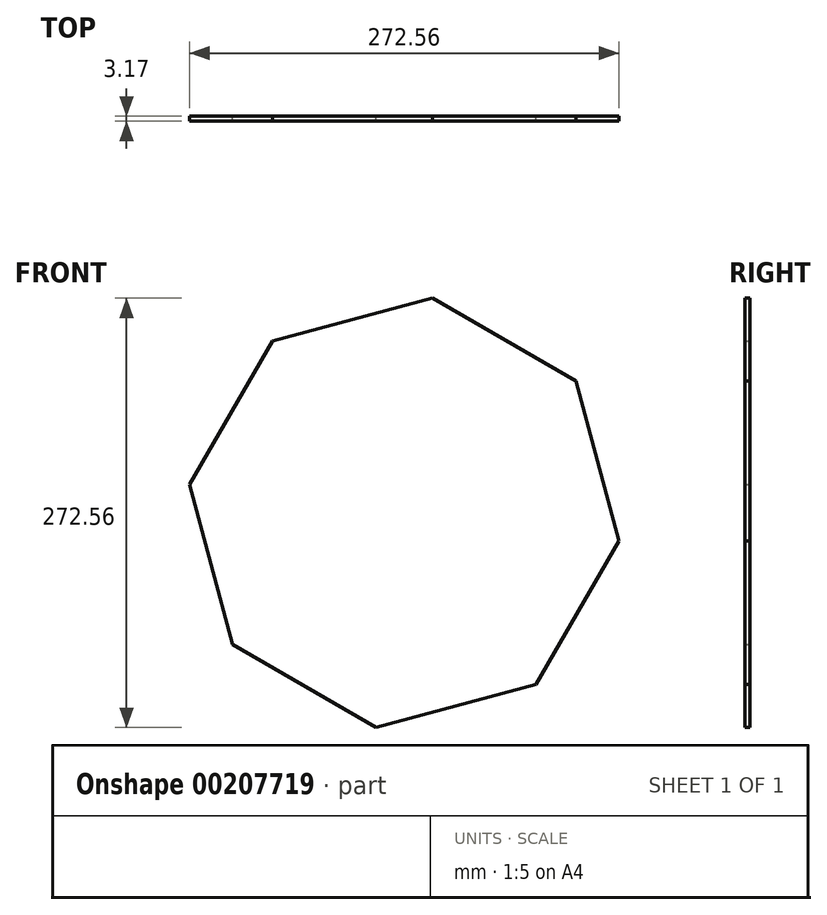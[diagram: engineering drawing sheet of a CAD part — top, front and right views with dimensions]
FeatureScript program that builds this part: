
annotation { "Feature Type Name" : "Feature", "Feature Type Description" : "" }
export const myFeature = defineFeature(function(context is Context, id is Id, definition is map)
    precondition{}
    {
        {
            var Q0;
            Q0=qCreatedBy(makeId("Front.planeOp"),FACE);
            var sketch = newSketch(context, id + "F0", { "sketchPlane" : qUnion([Q0])});
            skCircle(sketch, "E0.cCircle", {"center": v(0, 0) * mm, "radius": 127 * mm, "construction": true});
            skLineSegment(sketch, "E0.0", {"start": v(136.28, -17.98) * mm, "end": v(83.65, -109.08) * mm});
            skLineSegment(sketch, "E0.1", {"start": v(83.65, -109.08) * mm, "end": v(-17.98, -136.28) * mm});
            skLineSegment(sketch, "E0.2", {"start": v(-17.98, -136.28) * mm, "end": v(-109.08, -83.65) * mm});
            skLineSegment(sketch, "E0.3", {"start": v(-109.08, -83.65) * mm, "end": v(-136.28, 17.98) * mm});
            skLineSegment(sketch, "E0.4", {"start": v(-136.28, 17.98) * mm, "end": v(-83.65, 109.08) * mm});
            skLineSegment(sketch, "E0.5", {"start": v(-83.65, 109.08) * mm, "end": v(17.98, 136.28) * mm});
            skLineSegment(sketch, "E0.6", {"start": v(17.98, 136.28) * mm, "end": v(109.08, 83.65) * mm});
            skLineSegment(sketch, "E0.7", {"start": v(109.08, 83.65) * mm, "end": v(136.28, -17.98) * mm});
            skPoint(sketch, "E0.0.midPoint", {"position": v(109.97, -63.53) * mm});
            skSolve(sketch);
        }
        {
            var Q0;
            Q0 = qSketchRegion(id + "F0", true);
            extrude(context, id + "F1", {"entities" : qUnion([Q0]), "depth" : 3.17 * mm});
        }
    });
